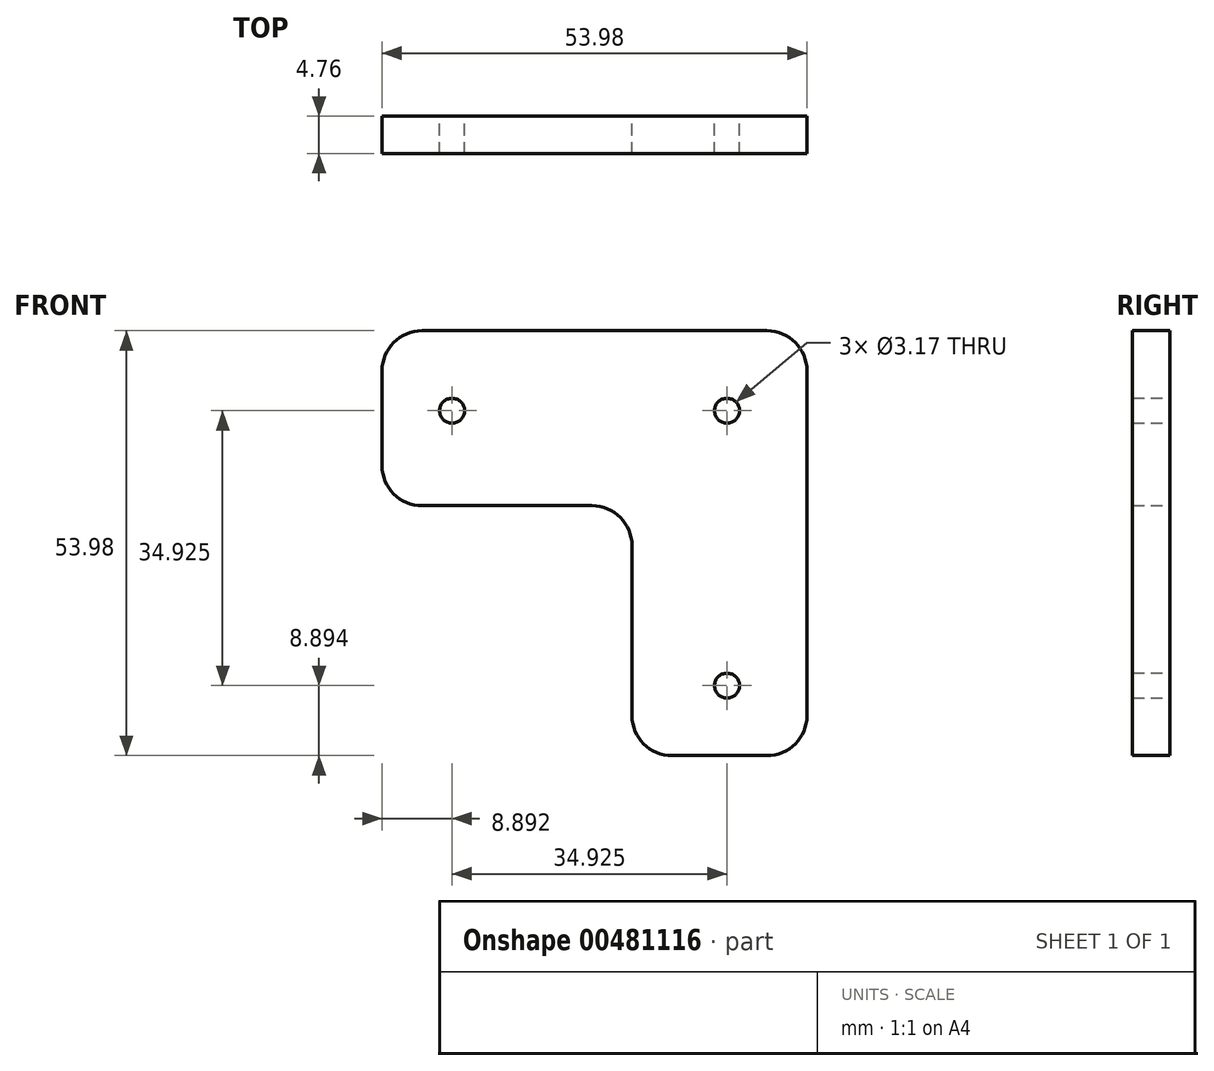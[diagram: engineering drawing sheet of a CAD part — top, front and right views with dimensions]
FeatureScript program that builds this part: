
annotation { "Feature Type Name" : "Feature", "Feature Type Description" : "" }
export const myFeature = defineFeature(function(context is Context, id is Id, definition is map)
    precondition{}
    {
        {
            var Q0;
            Q0=qCreatedBy(makeId("Front.planeOp"),FACE);
            var sketch = newSketch(context, id + "F0", { "sketchPlane" : qUnion([Q0])});
            skLineSegment(sketch, "E0", {"start": v(-22.1, 35.7) * mm, "end": v(31.88, 35.7) * mm});
            skLineSegment(sketch, "E1", {"start": v(31.88, 35.7) * mm, "end": v(31.88, -18.28) * mm});
            skLineSegment(sketch, "E2", {"start": v(31.88, -18.28) * mm, "end": v(9.65, -18.28) * mm});
            skLineSegment(sketch, "E3", {"start": v(9.65, -18.28) * mm, "end": v(9.65, 13.47) * mm});
            skLineSegment(sketch, "E4", {"start": v(9.65, 13.47) * mm, "end": v(-22.1, 13.47) * mm});
            skLineSegment(sketch, "E5", {"start": v(-22.1, 13.47) * mm, "end": v(-22.1, 35.7) * mm});
            skPoint(sketch, "E6.centerSnap0", {"position": v(20.76, -18.28) * mm});
            skPoint(sketch, "E7.centerSnap0", {"position": v(-22.1, 24.59) * mm});
            skCircle(sketch, "E8", {"center": v(21.72, 25.54) * mm, "radius": 1.59 * mm});
            skCircle(sketch, "E9", {"center": v(-13.2, 25.54) * mm, "radius": 1.59 * mm});
            skCircle(sketch, "E10", {"center": v(21.72, -9.39) * mm, "radius": 1.59 * mm});
            skSolve(sketch);
        }
        {
            var Q0;
            Q0=makeQuery(id+"F0.imprint","IMPRINT",FACE,{"disambiguationData":[TD([[makeQuery(id+"F0.imprint","IMPRINT",EDGE,{"derivedFrom":sQuery(id+"F0.wireOp",EDGE,"E0")}),-1.0]])]});
            extrude(context, id + "F1", {"entities" : qUnion([Q0]), "depth" : 4.76 * mm});
        }
        {
            var Q0;
            Q0=makeQuery(id+"F1.opExtrude","SWEPT_EDGE",EDGE,{"disambiguationData":[OSD([sQuery(id+"F0.wireOp",EDGE,"E0"),sQuery(id+"F0.wireOp",EDGE,"E5")])]});
            var Q1;
            Q1=makeQuery(id+"F1.opExtrude","SWEPT_EDGE",EDGE,{"disambiguationData":[OSD([sQuery(id+"F0.wireOp",EDGE,"E4"),sQuery(id+"F0.wireOp",EDGE,"E5")])]});
            var Q2;
            Q2=makeQuery(id+"F1.opExtrude","SWEPT_EDGE",EDGE,{"disambiguationData":[OSD([sQuery(id+"F0.wireOp",EDGE,"E2"),sQuery(id+"F0.wireOp",EDGE,"E3")])]});
            var Q3;
            Q3=makeQuery(id+"F1.opExtrude","SWEPT_EDGE",EDGE,{"disambiguationData":[OSD([sQuery(id+"F0.wireOp",EDGE,"E0"),sQuery(id+"F0.wireOp",EDGE,"E1")])]});
            var Q4;
            Q4=makeQuery(id+"F1.opExtrude","SWEPT_EDGE",EDGE,{"disambiguationData":[OSD([sQuery(id+"F0.wireOp",EDGE,"E1"),sQuery(id+"F0.wireOp",EDGE,"E2")])]});
            var Q5;
            Q5=makeQuery(id+"F1.opExtrude","SWEPT_EDGE",EDGE,{"disambiguationData":[OSD([sQuery(id+"F0.wireOp",EDGE,"E3"),sQuery(id+"F0.wireOp",EDGE,"E4")])]});
            fillet(context, id + "F2", {"entities" : qUnion([Q0, Q1, Q2, Q3, Q4, Q5]), "radius" : 5.08 * mm, "tangentPropagation" : true, "allowEdgeOverflow" : false});
        }
    });
